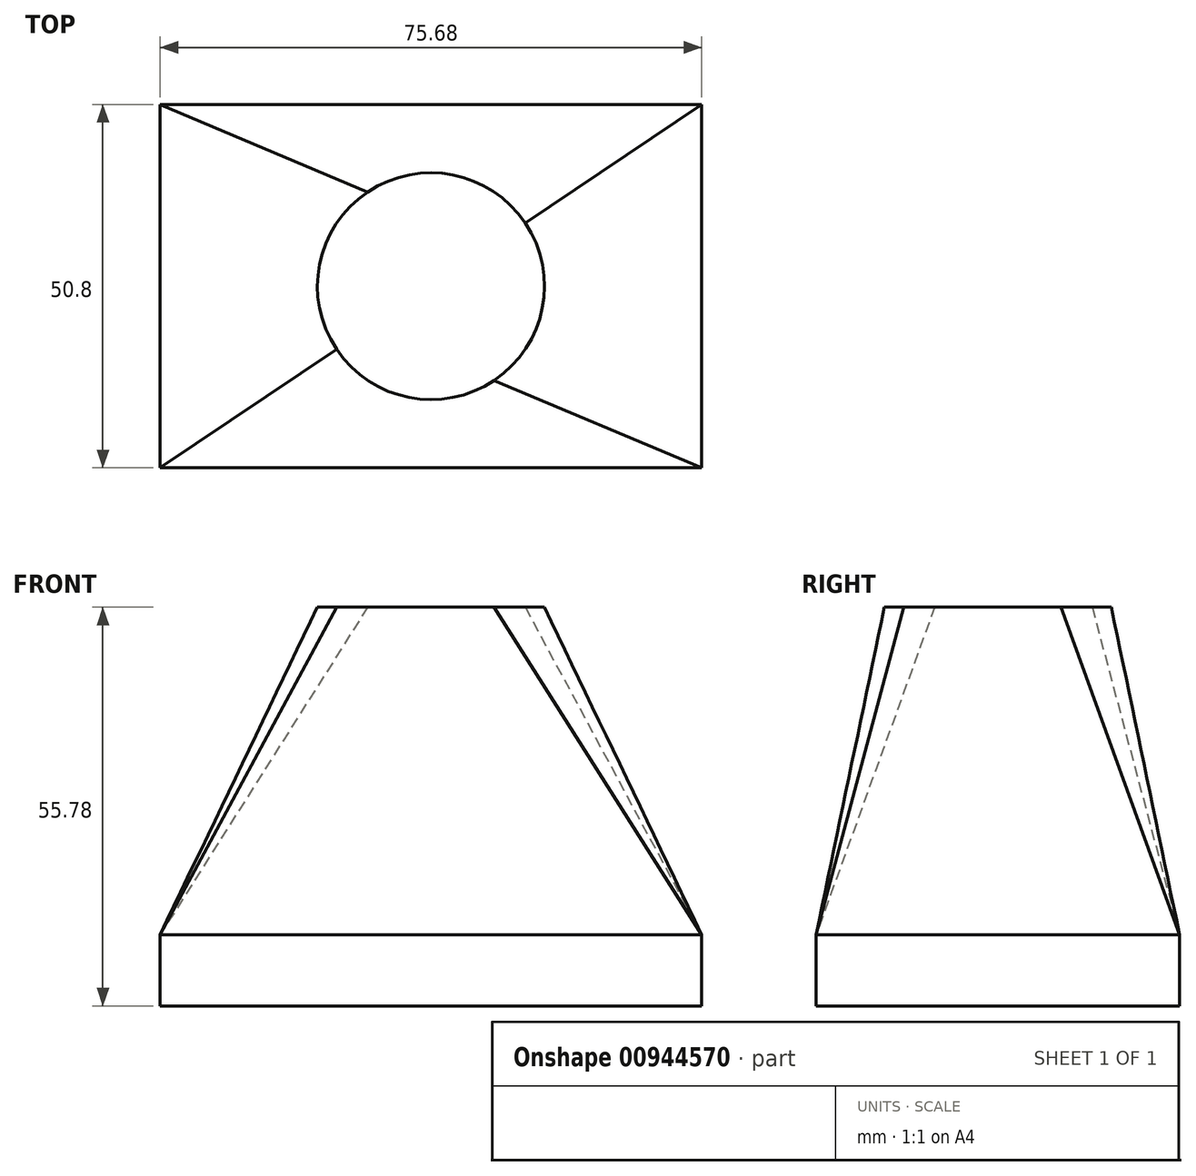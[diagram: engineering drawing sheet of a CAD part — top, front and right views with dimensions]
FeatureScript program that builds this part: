
annotation { "Feature Type Name" : "Feature", "Feature Type Description" : "" }
export const myFeature = defineFeature(function(context is Context, id is Id, definition is map)
    precondition{}
    {
        {
            var Q0;
            Q0=qCreatedBy(makeId("Front.planeOp"),FACE);
            var sketch = newSketch(context, id + "F0", { "sketchPlane" : qUnion([Q0])});
            skLineSegment(sketch, "E0.bottom", {"start": v(37.84, 4.98) * mm, "end": v(-37.84, 4.98) * mm});
            skLineSegment(sketch, "E0.top", {"start": v(37.84, -4.98) * mm, "end": v(-37.84, -4.98) * mm});
            skLineSegment(sketch, "E0.left", {"start": v(37.84, 4.98) * mm, "end": v(37.84, -4.98) * mm});
            skLineSegment(sketch, "E0.right", {"start": v(-37.84, 4.98) * mm, "end": v(-37.84, -4.98) * mm});
            skPoint(sketch, "E0.middle", {"position": v(0, 0) * mm});
            skSolve(sketch);
        }
        {
            var Q0;
            Q0 = qSketchRegion(id + "F0", true);
            extrude(context, id + "F1", {"entities" : qUnion([Q0]), "endBound" : BoundingType.SYMMETRIC, "depth" : 50.8 * mm, "offsetDistance" : 25.4 * mm});
        }
        {
            var Q0;
            Q0=qCreatedBy(makeId("Top.planeOp"),FACE);
            cPlane(context, id + "F2", {"entities" : qUnion([Q0]), "cplaneType" : CPlaneType.OFFSET, "offset" : 50.8 * mm, "width" : 152.4 * mm, "height" : 152.4 * mm});
        }
        {
            var Q0;
            Q0=qCreatedBy(id+"F2.planeOp",FACE);
            var sketch = newSketch(context, id + "F3", { "sketchPlane" : qUnion([Q0])});
            skCircle(sketch, "E1", {"center": v(0, 0) * mm, "radius": 15.86 * mm});
            skSolve(sketch);
        }
        {
            var Q1;
            Q1=makeQuery(id+"F3.imprint","IMPRINT",FACE,{"disambiguationData":[TD([[makeQuery(id+"F3.imprint","IMPRINT",EDGE,{"derivedFrom":sQuery(id+"F3.wireOp",EDGE,"E1")}),1.0]])]});
            var Q2;
            Q2=makeQuery(id+"F1.opExtrude","SWEPT_FACE",FACE,{"disambiguationData":[OSD([sQuery(id+"F0.wireOp",EDGE,"E0.bottom")])]});
            loft(context, id + "F4", {"operationType" : NewBodyOperationType.ADD, "sheetProfilesArray" : [{ "sheetProfileEntities" : qUnion([Q1]) }, { "sheetProfileEntities" : qUnion([Q2]) }]});
        }
    });
